# Revit family: Toilet_Tank-In_Wall-KOHLER-Next_Gen-K-28829_1
name_source: partatom
category: Plumbing Fixtures
units: mm (PartAtom-declared; Revit-internal decimal feet)

## family parameters
Cut with Voids When Loaded = No
Host = Face
OmniClass Number = 23.31.19.19.19
OmniClass Title = Water Closet Tanks
Part Type = Normal
Room Calculation Point = No
Round Connector Dimension = Use Diameter
Shared = No

## types (1)
- NA-Not Applicable
    ADA Compliant = No
    Assembly Code = D2010100
    CW Connection = Yes
    Cold Water Inlet = Cold Water Inlet
    Cold Water Outlet = Cold Water Outlet
    Date Modified = 02/02/2023
    Default Elevation = 0"
    Description = In Wall Tank Carrier 0.8/1.6
    Finish = Kohler-Plastic-0-White
    Flow Rate = 0 GPM
    Flush Rate- GPF = 1.6 GPF
    Flush Rate- LPF = 6.05LPF
    HW Connection = No
    Hot Water Inlet = Hot Water Inlet
    Length = 14 7/8"
    Manufacturer = Kohler Co.
    Master Format 2014 = 22 42 13.13
    Master Format 2014 Name = Residential Water Closets
    Material = Plastic
    Model = K-28829-NA
    Pressure = 0.00 psi
    Product Documentation Link = https://www.us.kohler.com
    Product Name = Next Gen
    Product Page URL = http://www.us.kohler.com
    Seat Included = No
    Secondary Finish = Kohler-Metal-Blue
    Type = 1
    URL = https://www.us.kohler.com
    Vent Connection = No
    Waste Connection = Yes
    Waste Water Inlet = Waste Water Inlet
    Waste Water Outlet = Waste Water Outlet
    WaterSense Certified = No
    Width = 20 1/2"

## geometry (parser evidence)
native form markers: Sweep x5
no freeform markers — native parametric forms only
